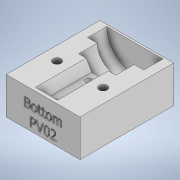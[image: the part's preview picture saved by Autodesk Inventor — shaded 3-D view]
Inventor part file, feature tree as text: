
AUTODESK INVENTOR PART (.ipt)
format: ipt  version: 2022.1 (Build 261234000, 234)  size: 1,094,656 bytes
history: native  units: in
note: dims shown in document units (in); Inventor stores cm internally (conversion verified against a paired STEP export)
features: sketch x6, extrude x4, reference x3, other x3, boolean_combine x1, emboss x1, hole x1, thicken_offset x1
ambient origin geometry x8: Origin, YZ Plane, XZ Plane, XY Plane, X Axis, Y Axis, Z Axis, Center Point
bodies: Solid6 (feature_tree), Solid8 (feature_tree), Solid1 (feature_tree)
feature tree (20):
  boolean_combine  "Combine2"
  extrude  "Extrusion6"  Depth=0.1in TaperAngle=0.0deg
  extrude  "Extrusion7"  Depth=0.1in
  extrude  "Extrusion8"  Depth=0.05in TaperAngle=0.0deg
  extrude  "Extrusion9"  Depth=0.375in
  emboss  "Emboss2"
  hole  "Hole4"  [1 undecoded]
  thicken_offset  "Thicken1"
  sketch  "Sketch9"  dims[d28=0.0in d29=0.0in d30=0.1in d31=0.0in]
  sketch  "Sketch10"  dims[d32=0.0in d33=0.0in d34=0.1in]
  sketch  "Sketch11"  dims[d35=0.0in d36=0.0in d53=0.05in d54=0.0in]
  sketch  "Sketch12"  dims[d55=0.375in d56=0.375in]
  sketch  "Sketch15"  dims[d57=1.0in d58=1.0in]
  sketch  "Sketch16"  dims[d59=0.185in d60=0.75in d61=0.2173in d62=0.22in d63=0.5635in d64=1.0in d65=0.8108in d66=0.01in d67=0.01in]
  reference  "Reference1"
  reference  "Reference2"
  reference  "Reference3"
  other  "Solid1:1"
  other  "jigForHexBushing.iam"
  other  "jigForHexBushingForConnectorPieceTop:1"
note: 1 required parameter value undecoded (feature->parameter linkage not recoverable at this tier; creation-order binding heuristic only, values carry confidence <= 0.55)
